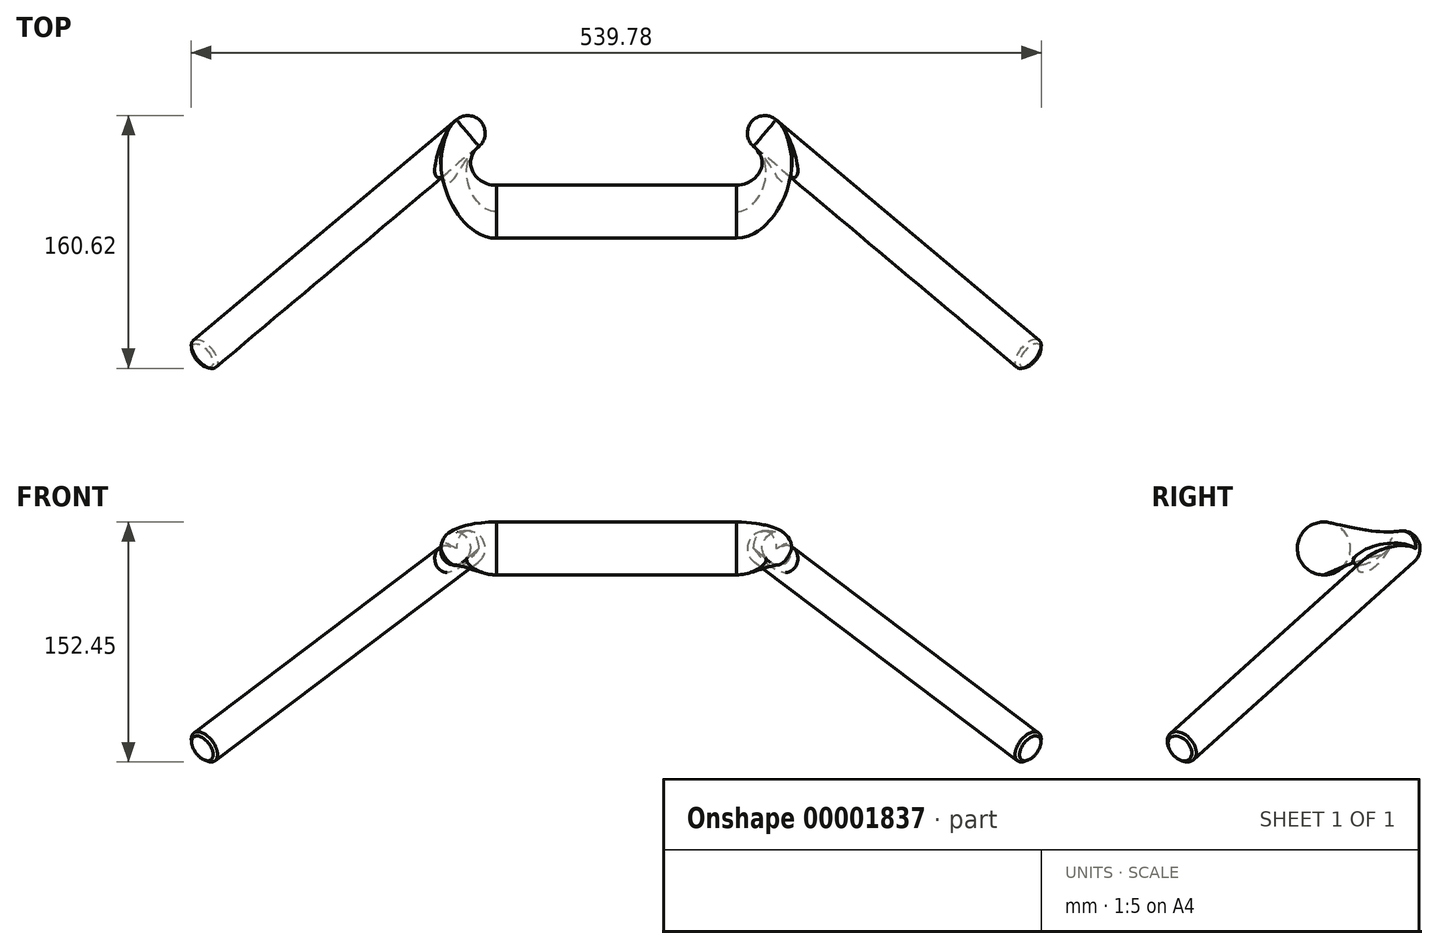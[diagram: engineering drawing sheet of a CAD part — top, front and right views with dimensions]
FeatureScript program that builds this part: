
annotation { "Feature Type Name" : "Feature", "Feature Type Description" : "" }
export const myFeature = defineFeature(function(context is Context, id is Id, definition is map)
    precondition{}
    {
        {
            var Q0;
            Q0=qCreatedBy(makeId("Top.planeOp"),FACE);
            var sketch = newSketch(context, id + "F0", { "sketchPlane" : qUnion([Q0])});
            skLineSegment(sketch, "E0", {"start": v(0, 0) * mm, "end": v(0, 51.2) * mm, "construction": true});
            skLineSegment(sketch, "E1", {"start": v(0, 0) * mm, "end": v(-76.2, 0) * mm});
            skArc(sketch, "E2", {"start": v(-94.4, 50) * mm, "mid": v(-102.8, 18.63) * mm, "end": v(-76.2, 0) * mm});
            skLineSegment(sketch, "E3", {"start": v(-101.92, 58.97) * mm, "end": v(-86.87, 41.03) * mm, "construction": true});
            skLineSegment(sketch, "E4", {"start": v(-94.4, 50) * mm, "end": v(-127, 22.64) * mm, "construction": true});
            skSolve(sketch);
        }
        {
            var Q0;
            Q0=sQuery(id+"F0.wireOp",EDGE,"E3");
            cPlane(context, id + "F1", {"entities" : qUnion([Q0]), "cplaneType" : CPlaneType.LINE_ANGLE, "offset" : 25 * mm, "angle" : 30 * degree, "width" : 150 * mm, "height" : 150 * mm});
        }
        {
            var Q0;
            Q0=qCreatedBy(id+"F1.planeOp",FACE);
            var sketch = newSketch(context, id + "F2", { "sketchPlane" : qUnion([Q0])});
            skLineSegment(sketch, "E5", {"start": v(-93.86, -46.88) * mm, "end": v(-276.28, 129.87) * mm});
            skSolve(sketch);
        }
        {
            var Q0;
            Q0=sQuery(id+"F2.wireOp",VERTEX,"E5.end");
            var Q1;
            Q1=sQuery(id+"F2.wireOp",EDGE,"E5");
            cPlane(context, id + "F3", {"entities" : qUnion([Q0, Q1]), "cplaneType" : CPlaneType.LINE_POINT, "offset" : 25 * mm, "width" : 150 * mm, "height" : 150 * mm});
        }
        {
            var Q0;
            Q0=qCreatedBy(id+"F3.planeOp",FACE);
            var sketch = newSketch(context, id + "F4", { "sketchPlane" : qUnion([Q0])});
            skCircle(sketch, "E6", {"center": v(-83.5, 56.82) * mm, "radius": 11.11 * mm});
            skLineSegment(sketch, "E7", {"start": v(-94.61, 56.82) * mm, "end": v(-72.39, 56.82) * mm});
            skSolve(sketch);
        }
        {
            var Q0;
            Q0=qCreatedBy(makeId("Right.planeOp"),FACE);
            var sketch = newSketch(context, id + "F5", { "sketchPlane" : qUnion([Q0])});
            skCircle(sketch, "E8", {"center": v(0, 0) * mm, "radius": 16.83 * mm});
            skSolve(sketch);
        }
        {
            var Q0;
            Q0=makeQuery(id+"F5.imprint","IMPRINT",FACE,{"disambiguationData":[TD([[makeQuery(id+"F5.imprint","IMPRINT",EDGE,{"derivedFrom":sQuery(id+"F5.wireOp",EDGE,"E8")}),1.0]])]});
            var Q1;
            Q1=sQuery(id+"F0.wireOp",EDGE,"E1");
            sweep(context, id + "F6", {"profiles" : qUnion([Q0]), "path" : qUnion([Q1])});
        }
        {
            var Q0;
            Q0=sQuery(id+"F0.wireOp",EDGE,"E2");
            var Q1;
            Q1=sQuery(id+"F0.wireOp",VERTEX,"E4.start");
            cPlane(context, id + "F7", {"entities" : qUnion([Q0, Q1]), "cplaneType" : CPlaneType.CURVE_POINT, "offset" : 25 * mm, "width" : 150 * mm, "height" : 150 * mm});
        }
        {
            var Q0;
            Q0=qCreatedBy(id+"F7.planeOp",FACE);
            var sketch = newSketch(context, id + "F8", { "sketchPlane" : qUnion([Q0])});
            skCircle(sketch, "E9", {"center": v(-98.98, 0) * mm, "radius": 11.11 * mm});
            skSolve(sketch);
        }
        {
            var Q1;
            Q1=makeQuery(id+"F6.opSweep","CAP_FACE",FACE,{"disambiguationData":[OSD([sQuery(id+"F0.wireOp",VERTEX,"E1.end"),sQuery(id+"F5.wireOp",EDGE,"E8")])],"isStart":false});
            var Q2;
            Q2=makeQuery(id+"F8.imprint","IMPRINT",FACE,{"disambiguationData":[TD([[makeQuery(id+"F8.imprint","IMPRINT",EDGE,{"derivedFrom":sQuery(id+"F8.wireOp",EDGE,"E9")}),1.0]])]});
            var Q3;
            Q3=sQuery(id+"F0.wireOp",EDGE,"E2");
            var Q4;
            Q4=sQuery(id+"F8.wireOp",VERTEX,"E9.center");
            var Q5;
            Q5=sQuery(id+"F0.wireOp",VERTEX,"E2.end");
            loft(context, id + "F9", {"operationType" : NewBodyOperationType.ADD, "startCondition" : LoftEndDerivativeType.NORMAL_TO_PROFILE, "startMagnitude" : 3, "endCondition" : LoftEndDerivativeType.NORMAL_TO_PROFILE, "endMagnitude" : 3, "sheetProfilesArray" : [{ "sheetProfileEntities" : qUnion([Q1]) }, { "sheetProfileEntities" : qUnion([Q2]) }], "guidesArray" : [{ "guideEntities" : qUnion([Q3]), "guideDerivativeType" : LoftGuideDerivativeType.DEFAULT, "guideDerivativeMagnitude" : 1 }], "connections" : [{ "connectionEntities" : qUnion([Q4, Q5]), "connectionEdgeQueries" : qUnion([]), "connectionEdgeParameters" : [] }]});
        }
        {
            var Q0;
            Q0=makeQuery(id+"F4.imprint","IMPRINT",FACE,{"disambiguationData":[TD([[makeQuery(id+"F4.imprint","IMPRINT",EDGE,{"derivedFrom":sQuery(id+"F4.wireOp",EDGE,"E6")}),1.0]])]});
            var Q1;
            Q1=sQuery(id+"F2.wireOp",EDGE,"E5");
            sweep(context, id + "F10", {"operationType" : NewBodyOperationType.ADD, "profiles" : qUnion([Q0]), "path" : qUnion([Q1])});
        }
        {
            var Q0;
            Q0=makeQuery(id+"F10.opSweep","CAP_FACE",FACE,{"disambiguationData":[OSD([sQuery(id+"F2.wireOp",VERTEX,"E5.start"),sQuery(id+"F4.wireOp",EDGE,"E6")])],"isStart":false});
            var Q1;
            Q1=sQuery(id+"F0.wireOp",EDGE,"E3");
            revolve(context, id + "F11", {"operationType" : NewBodyOperationType.ADD, "entities" : qUnion([Q0]), "axis" : qUnion([Q1]), "revolveType" : RevolveType.ONE_DIRECTION, "angle" : 150 * degree});
        }
        {
            var Q0;
            Q0=makeQuery(id+"F10.boolean.opBoolean","INTERSECT",EDGE,{"derivedFrom":[makeQuery(id+"F9.opLoft","SWEPT_FACE",FACE,{"disambiguationData":[OSD([sQuery(id+"F0.wireOp",VERTEX,"E1.end"),sQuery(id+"F5.wireOp",EDGE,"E8"),sQuery(id+"F8.wireOp",EDGE,"E9")])]}),makeQuery(id+"F10.opSweep","SWEPT_FACE",FACE,{"disambiguationData":[OSD([sQuery(id+"F2.wireOp",EDGE,"E5"),sQuery(id+"F4.wireOp",EDGE,"E6")])]})]});
            fillet(context, id + "F12", {"entities" : qUnion([Q0]), "radius" : 5 * mm, "tangentPropagation" : true, "allowEdgeOverflow" : false});
        }
        {
            var Q0;
            Q0=makeQuery(id+"F10.opSweep","CAP_EDGE",EDGE,{"disambiguationData":[OSD([sQuery(id+"F2.wireOp",VERTEX,"E5.end"),sQuery(id+"F4.wireOp",EDGE,"E6")])],"isStart":true});
            chamfer(context, id + "F13", {"entities" : qUnion([Q0]), "width" : 2 * mm, "tangentPropagation" : true});
        }
        {
            var Q0;
            Q0=makeQuery(id+"F6.opSweep","SWEPT_BODY",BODY,{"disambiguationData":[OSD([sQuery(id+"F0.wireOp",EDGE,"E1"),sQuery(id+"F5.wireOp",EDGE,"E8")])]});
            var Q1;
            Q1=qCreatedBy(makeId("Right.planeOp"),FACE);
            mirror(context, id + "F14", {"operationType" : NewBodyOperationType.ADD, "entities" : qUnion([Q0]), "mirrorPlane" : qUnion([Q1])});
        }
    });
